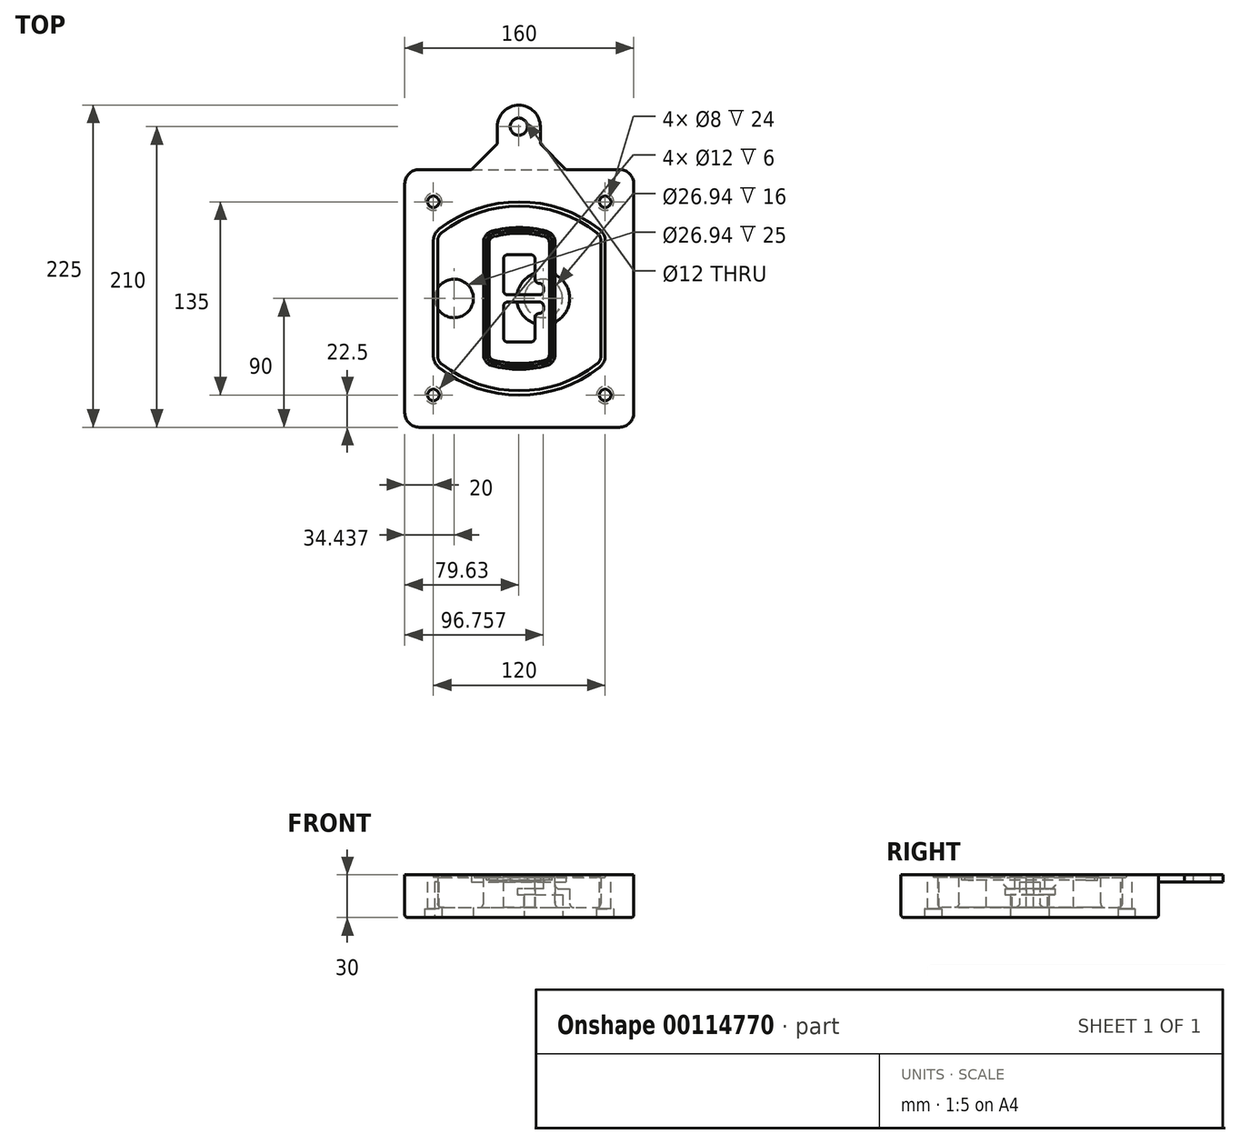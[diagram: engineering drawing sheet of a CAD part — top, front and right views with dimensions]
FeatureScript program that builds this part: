
annotation { "Feature Type Name" : "Feature", "Feature Type Description" : "" }
export const myFeature = defineFeature(function(context is Context, id is Id, definition is map)
    precondition{}
    {
        {
            var Q0;
            Q0=qCreatedBy(makeId("Top.planeOp"),FACE);
            var sketch = newSketch(context, id + "F0", { "sketchPlane" : qUnion([Q0])});
            skPoint(sketch, "E0.rect.middle", {"position": v(0, 0) * mm});
            skLineSegment(sketch, "E1.bottom", {"start": v(-70, -90) * mm, "end": v(70, -90) * mm});
            skLineSegment(sketch, "E1.top", {"start": v(-70, 90) * mm, "end": v(70, 90) * mm});
            skLineSegment(sketch, "E1.left", {"start": v(-80, -80) * mm, "end": v(-80, 80) * mm});
            skLineSegment(sketch, "E1.right", {"start": v(80, -80) * mm, "end": v(80, 80) * mm});
            skLineSegment(sketch, "E2", {"start": v(-80, 90) * mm, "end": v(80, -90) * mm, "construction": true});
            skLineSegment(sketch, "E3", {"start": v(80, 90) * mm, "end": v(-80, -90) * mm, "construction": true});
            skCircle(sketch, "E4", {"center": v(-60, 67.5) * mm, "radius": 4 * mm});
            skCircle(sketch, "E5", {"center": v(60, 67.5) * mm, "radius": 4 * mm});
            skCircle(sketch, "E6", {"center": v(60, -67.5) * mm, "radius": 4 * mm});
            skCircle(sketch, "E7", {"center": v(-60, -67.5) * mm, "radius": 4 * mm});
            skLineSegment(sketch, "E8", {"start": v(-60, 67.5) * mm, "end": v(60, 67.5) * mm, "construction": true});
            skLineSegment(sketch, "E9", {"start": v(60, 67.5) * mm, "end": v(60, -67.5) * mm, "construction": true});
            skLineSegment(sketch, "E10", {"start": v(60, -67.5) * mm, "end": v(-60, -67.5) * mm, "construction": true});
            skLineSegment(sketch, "E11", {"start": v(-60, -67.5) * mm, "end": v(-60, 67.5) * mm, "construction": true});
            skLineSegment(sketch, "E12", {"start": v(-60, 40.3) * mm, "end": v(-60, -40.3) * mm});
            skLineSegment(sketch, "E13", {"start": v(60, 40.3) * mm, "end": v(60, -40.3) * mm});
            skArc(sketch, "E14", {"start": v(56.15, 48.18) * mm, "mid": v(0, 67.5) * mm, "end": v(-56.15, 48.18) * mm});
            skArc(sketch, "E15", {"start": v(-56.15, -48.18) * mm, "mid": v(0, -67.5) * mm, "end": v(56.15, -48.18) * mm});
            skLineSegment(sketch, "E16", {"start": v(-60, 0) * mm, "end": v(60, 0) * mm, "construction": true});
            skPoint(sketch, "E17.visualSharp", {"position": v(-60, -45) * mm});
            skArc(sketch, "E17.filletArc", {"start": v(-60, -40.3) * mm, "mid": v(-58.99, -44.68) * mm, "end": v(-56.15, -48.18) * mm});
            skPoint(sketch, "E18.visualSharp", {"position": v(-60, 45) * mm});
            skArc(sketch, "E18.filletArc", {"start": v(-56.15, 48.18) * mm, "mid": v(-58.99, 44.68) * mm, "end": v(-60, 40.3) * mm});
            skPoint(sketch, "E19.visualSharp", {"position": v(60, 45) * mm});
            skArc(sketch, "E19.filletArc", {"start": v(60, 40.3) * mm, "mid": v(58.99, 44.68) * mm, "end": v(56.15, 48.18) * mm});
            skPoint(sketch, "E20.visualSharp", {"position": v(60, -45) * mm});
            skArc(sketch, "E20.filletArc", {"start": v(56.15, -48.18) * mm, "mid": v(58.99, -44.68) * mm, "end": v(60, -40.3) * mm});
            skPoint(sketch, "E21.visualSharp", {"position": v(-80, 90) * mm});
            skArc(sketch, "E21.filletArc", {"start": v(-70, 90) * mm, "mid": v(-77.07, 87.07) * mm, "end": v(-80, 80) * mm});
            skPoint(sketch, "E22.visualSharp", {"position": v(80, 90) * mm});
            skArc(sketch, "E22.filletArc", {"start": v(80, 80) * mm, "mid": v(77.07, 87.07) * mm, "end": v(70, 90) * mm});
            skPoint(sketch, "E23.visualSharp", {"position": v(80, -90) * mm});
            skArc(sketch, "E23.filletArc", {"start": v(70, -90) * mm, "mid": v(77.07, -87.07) * mm, "end": v(80, -80) * mm});
            skPoint(sketch, "E24.visualSharp", {"position": v(-80, -90) * mm});
            skArc(sketch, "E24.filletArc", {"start": v(-80, -80) * mm, "mid": v(-77.07, -87.07) * mm, "end": v(-70, -90) * mm});
            skArc(sketch, "E25.0", {"start": v(57, 40.3) * mm, "mid": v(56.3, 43.36) * mm, "end": v(54.3, 45.81) * mm});
            skLineSegment(sketch, "E25.1", {"start": v(57, 40.3) * mm, "end": v(57, -40.3) * mm});
            skArc(sketch, "E25.2", {"start": v(54.3, -45.81) * mm, "mid": v(56.3, -43.36) * mm, "end": v(57, -40.3) * mm});
            skArc(sketch, "E25.3", {"start": v(-54.3, -45.81) * mm, "mid": v(0, -64.5) * mm, "end": v(54.3, -45.81) * mm});
            skArc(sketch, "E25.4", {"start": v(-57, -40.3) * mm, "mid": v(-56.3, -43.36) * mm, "end": v(-54.3, -45.81) * mm});
            skArc(sketch, "E25.5", {"start": v(54.3, 45.81) * mm, "mid": v(0, 64.5) * mm, "end": v(-54.3, 45.81) * mm});
            skLineSegment(sketch, "E25.6", {"start": v(-57, 40.3) * mm, "end": v(-57, -40.3) * mm});
            skArc(sketch, "E25.7", {"start": v(-54.3, 45.81) * mm, "mid": v(-56.3, 43.36) * mm, "end": v(-57, 40.3) * mm});
            skArc(sketch, "E26.0", {"start": v(-58.62, 51.33) * mm, "mid": v(-62.58, 46.43) * mm, "end": v(-64, 40.3) * mm});
            skArc(sketch, "E26.1", {"start": v(58.62, 51.33) * mm, "mid": v(0, 71.5) * mm, "end": v(-58.62, 51.33) * mm});
            skArc(sketch, "E26.2", {"start": v(64, 40.3) * mm, "mid": v(62.58, 46.43) * mm, "end": v(58.62, 51.33) * mm});
            skLineSegment(sketch, "E26.3", {"start": v(64, 40.3) * mm, "end": v(64, -40.3) * mm});
            skArc(sketch, "E26.4", {"start": v(58.62, -51.33) * mm, "mid": v(62.58, -46.43) * mm, "end": v(64, -40.3) * mm});
            skLineSegment(sketch, "E26.5", {"start": v(-64, 40.3) * mm, "end": v(-64, -40.3) * mm});
            skArc(sketch, "E26.6", {"start": v(-58.62, -51.33) * mm, "mid": v(0, -71.5) * mm, "end": v(58.62, -51.33) * mm});
            skArc(sketch, "E26.7", {"start": v(-64, -40.3) * mm, "mid": v(-62.58, -46.43) * mm, "end": v(-58.62, -51.33) * mm});
            skSolve(sketch);
        }
        {
            var Q0;
            Q0=makeQuery(id+"F0.imprint","IMPRINT",FACE,{"disambiguationData":[TD([[makeQuery(id+"F0.imprint","IMPRINT",EDGE,{"derivedFrom":sQuery(id+"F0.wireOp",EDGE,"E1.bottom")}),1.0]])]});
            var Q1;
            Q1=makeQuery(id+"F0.imprint","IMPRINT",FACE,{"disambiguationData":[TD([[makeQuery(id+"F0.imprint","IMPRINT",EDGE,{"derivedFrom":sQuery(id+"F0.wireOp",EDGE,"E12")}),1.0]])]});
            var Q2;
            Q2=makeQuery(id+"F0.imprint","IMPRINT",FACE,{"disambiguationData":[TD([[makeQuery(id+"F0.imprint","IMPRINT",EDGE,{"derivedFrom":sQuery(id+"F0.wireOp",EDGE,"E25.0")}),1.0]])]});
            var Q3;
            Q3=makeQuery(id+"F0.imprint","IMPRINT",FACE,{"disambiguationData":[TD([[makeQuery(id+"F0.imprint","IMPRINT",EDGE,{"derivedFrom":sQuery(id+"F0.wireOp",EDGE,"E12")}),-1.0]])]});
            var Q4;
            Q4 = qSketchRegion(id + "F16", true);
            extrude(context, id + "F1", {"entities" : qUnion([Q0, Q1, Q2, Q3, Q4]), "oppositeDirection" : true, "depth" : 25 * mm});
        }
        {
            var Q0;
            Q0=makeQuery(id+"F0.imprint","IMPRINT",FACE,{"disambiguationData":[TD([[makeQuery(id+"F0.imprint","IMPRINT",EDGE,{"derivedFrom":sQuery(id+"F0.wireOp",EDGE,"E12")}),1.0]])]});
            extrude(context, id + "F2", {"entities" : qUnion([Q0]), "operationType" : NewBodyOperationType.ADD, "depth" : 3 * mm});
        }
        {
            var Q0;
            Q0=makeQuery(id+"F0.imprint","IMPRINT",FACE,{"disambiguationData":[TD([[makeQuery(id+"F0.imprint","IMPRINT",EDGE,{"derivedFrom":sQuery(id+"F0.wireOp",EDGE,"E25.0")}),1.0]])]});
            extrude(context, id + "F3", {"entities" : qUnion([Q0]), "operationType" : NewBodyOperationType.REMOVE, "oppositeDirection" : true, "depth" : 18 * mm});
        }
        {
            var Q0;
            Q0=makeQuery(id+"F2.opExtrude","CAP_FACE",FACE,{"disambiguationData":[OSD([sQuery(id+"F0.wireOp",EDGE,"E12"),sQuery(id+"F0.wireOp",EDGE,"E13"),sQuery(id+"F0.wireOp",EDGE,"E14"),sQuery(id+"F0.wireOp",EDGE,"E15"),sQuery(id+"F0.wireOp",EDGE,"E17.filletArc"),sQuery(id+"F0.wireOp",EDGE,"E18.filletArc"),sQuery(id+"F0.wireOp",EDGE,"E19.filletArc"),sQuery(id+"F0.wireOp",EDGE,"E20.filletArc"),sQuery(id+"F0.wireOp",EDGE,"E25.0"),sQuery(id+"F0.wireOp",EDGE,"E25.1"),sQuery(id+"F0.wireOp",EDGE,"E25.2"),sQuery(id+"F0.wireOp",EDGE,"E25.3"),sQuery(id+"F0.wireOp",EDGE,"E25.4"),sQuery(id+"F0.wireOp",EDGE,"E25.5"),sQuery(id+"F0.wireOp",EDGE,"E25.6"),sQuery(id+"F0.wireOp",EDGE,"E25.7")])],"isStart":false});
            var sketch = newSketch(context, id + "F4", { "sketchPlane" : qUnion([Q0])});
            skArc(sketch, "E27.0", {"start": v(-19.08, -46.97) * mm, "mid": v(0, -49.5) * mm, "end": v(19.08, -46.97) * mm});
            skArc(sketch, "E28.0", {"start": v(19.08, 46.97) * mm, "mid": v(0, 49.5) * mm, "end": v(-19.08, 46.97) * mm});
            skLineSegment(sketch, "E29", {"start": v(-25, 39.25) * mm, "end": v(-25, -39.25) * mm});
            skLineSegment(sketch, "E30", {"start": v(25, 39.25) * mm, "end": v(25, -39.25) * mm});
            skLineSegment(sketch, "E31", {"start": v(-25, 45.1) * mm, "end": v(25, 45.1) * mm, "construction": true});
            skLineSegment(sketch, "E32", {"start": v(-25, -45.1) * mm, "end": v(25, -45.1) * mm, "construction": true});
            skPoint(sketch, "E33.visualSharp", {"position": v(-25, 45.1) * mm});
            skArc(sketch, "E33.filletArc", {"start": v(-19.08, 46.97) * mm, "mid": v(-23.35, 44.11) * mm, "end": v(-25, 39.25) * mm});
            skPoint(sketch, "E34.visualSharp", {"position": v(25, 45.1) * mm});
            skArc(sketch, "E34.filletArc", {"start": v(25, 39.25) * mm, "mid": v(23.35, 44.11) * mm, "end": v(19.08, 46.97) * mm});
            skPoint(sketch, "E35.visualSharp", {"position": v(25, -45.1) * mm});
            skArc(sketch, "E35.filletArc", {"start": v(19.08, -46.97) * mm, "mid": v(23.35, -44.11) * mm, "end": v(25, -39.25) * mm});
            skPoint(sketch, "E36.visualSharp", {"position": v(-25, -45.1) * mm});
            skArc(sketch, "E36.filletArc", {"start": v(-25, -39.25) * mm, "mid": v(-23.35, -44.11) * mm, "end": v(-19.08, -46.97) * mm});
            skArc(sketch, "E37.0", {"start": v(54.3, 45.81) * mm, "mid": v(0, 64.5) * mm, "end": v(-54.3, 45.81) * mm});
            skArc(sketch, "E37.1", {"start": v(-54.3, 45.81) * mm, "mid": v(-56.3, 43.36) * mm, "end": v(-57, 40.3) * mm});
            skLineSegment(sketch, "E37.2", {"start": v(-57, 40.3) * mm, "end": v(-57, -40.3) * mm});
            skArc(sketch, "E37.3", {"start": v(-57, -40.3) * mm, "mid": v(-56.3, -43.36) * mm, "end": v(-54.3, -45.81) * mm});
            skArc(sketch, "E37.4", {"start": v(-54.3, -45.81) * mm, "mid": v(0, -64.5) * mm, "end": v(54.3, -45.81) * mm});
            skArc(sketch, "E37.5", {"start": v(54.3, -45.81) * mm, "mid": v(56.3, -43.36) * mm, "end": v(57, -40.3) * mm});
            skLineSegment(sketch, "E37.6", {"start": v(57, 40.3) * mm, "end": v(57, -40.3) * mm});
            skArc(sketch, "E37.7", {"start": v(57, 40.3) * mm, "mid": v(56.3, 43.36) * mm, "end": v(54.3, 45.81) * mm});
            skLineSegment(sketch, "E38.0", {"start": v(23, 39.25) * mm, "end": v(23, -39.25) * mm});
            skArc(sketch, "E38.1", {"start": v(18.56, -45.04) * mm, "mid": v(21.76, -42.9) * mm, "end": v(23, -39.25) * mm});
            skArc(sketch, "E38.2", {"start": v(-18.56, -45.04) * mm, "mid": v(0, -47.5) * mm, "end": v(18.56, -45.04) * mm});
            skArc(sketch, "E38.3", {"start": v(-23, -39.25) * mm, "mid": v(-21.76, -42.9) * mm, "end": v(-18.56, -45.04) * mm});
            skLineSegment(sketch, "E38.4", {"start": v(-23, 39.25) * mm, "end": v(-23, -39.25) * mm});
            skArc(sketch, "E38.5", {"start": v(23, 39.25) * mm, "mid": v(21.76, 42.9) * mm, "end": v(18.56, 45.04) * mm});
            skArc(sketch, "E38.6", {"start": v(-18.56, 45.04) * mm, "mid": v(-21.76, 42.9) * mm, "end": v(-23, 39.25) * mm});
            skArc(sketch, "E38.7", {"start": v(18.56, 45.04) * mm, "mid": v(0, 47.5) * mm, "end": v(-18.56, 45.04) * mm});
            skArc(sketch, "E39.0", {"start": v(21, 39.25) * mm, "mid": v(20.18, 41.68) * mm, "end": v(18.04, 43.1) * mm});
            skLineSegment(sketch, "E39.1", {"start": v(21, 39.25) * mm, "end": v(21, -39.25) * mm});
            skArc(sketch, "E39.2", {"start": v(18.04, -43.1) * mm, "mid": v(20.18, -41.68) * mm, "end": v(21, -39.25) * mm});
            skArc(sketch, "E39.3", {"start": v(-18.04, -43.1) * mm, "mid": v(0, -45.5) * mm, "end": v(18.04, -43.1) * mm});
            skArc(sketch, "E39.4", {"start": v(-21, -39.25) * mm, "mid": v(-20.18, -41.68) * mm, "end": v(-18.04, -43.1) * mm});
            skArc(sketch, "E39.5", {"start": v(18.04, 43.1) * mm, "mid": v(0, 45.5) * mm, "end": v(-18.04, 43.1) * mm});
            skLineSegment(sketch, "E39.6", {"start": v(-21, 39.25) * mm, "end": v(-21, -39.25) * mm});
            skArc(sketch, "E39.7", {"start": v(-18.04, 43.1) * mm, "mid": v(-20.18, 41.68) * mm, "end": v(-21, 39.25) * mm});
            skLineSegment(sketch, "E40", {"start": v(-25, 0) * mm, "end": v(25, 0) * mm, "construction": true});
            skLineSegment(sketch, "E41", {"start": v(-11, 5.5) * mm, "end": v(-11, 27.5) * mm});
            skLineSegment(sketch, "E42", {"start": v(-8, 30.5) * mm, "end": v(8, 30.5) * mm});
            skLineSegment(sketch, "E43", {"start": v(11, 27.5) * mm, "end": v(11, 13.5) * mm});
            skLineSegment(sketch, "E44", {"start": v(14, 10.5) * mm, "end": v(14, 10.5) * mm});
            skLineSegment(sketch, "E45", {"start": v(17, 7.5) * mm, "end": v(17, 5.5) * mm});
            skLineSegment(sketch, "E46", {"start": v(14, 2.5) * mm, "end": v(-8, 2.5) * mm});
            skPoint(sketch, "E47.visualSharp", {"position": v(-11, 30.5) * mm});
            skArc(sketch, "E47.filletArc", {"start": v(-8, 30.5) * mm, "mid": v(-10.12, 29.62) * mm, "end": v(-11, 27.5) * mm});
            skPoint(sketch, "E48.visualSharp", {"position": v(11, 30.5) * mm});
            skArc(sketch, "E48.filletArc", {"start": v(11, 27.5) * mm, "mid": v(10.12, 29.62) * mm, "end": v(8, 30.5) * mm});
            skPoint(sketch, "E49.visualSharp", {"position": v(11, 10.5) * mm});
            skArc(sketch, "E49.filletArc", {"start": v(11, 13.5) * mm, "mid": v(11.88, 11.38) * mm, "end": v(14, 10.5) * mm});
            skPoint(sketch, "E50.visualSharp", {"position": v(17, 10.5) * mm});
            skArc(sketch, "E50.filletArc", {"start": v(17, 7.5) * mm, "mid": v(16.12, 9.62) * mm, "end": v(14, 10.5) * mm});
            skPoint(sketch, "E51.visualSharp", {"position": v(17, 2.5) * mm});
            skArc(sketch, "E51.filletArc", {"start": v(14, 2.5) * mm, "mid": v(16.12, 3.38) * mm, "end": v(17, 5.5) * mm});
            skPoint(sketch, "E52.visualSharp", {"position": v(-11, 2.5) * mm});
            skArc(sketch, "E52.filletArc", {"start": v(-11, 5.5) * mm, "mid": v(-10.12, 3.38) * mm, "end": v(-8, 2.5) * mm});
            skLineSegment(sketch, "E53.0.MirrorCS", {"start": v(14, -2.5) * mm, "end": v(-8, -2.5) * mm});
            skArc(sketch, "E54.0.MirrorCS", {"start": v(-11, -5.5) * mm, "mid": v(-10.12, -3.38) * mm, "end": v(-8, -2.5) * mm});
            skLineSegment(sketch, "E55.0.MirrorCS", {"start": v(-11, -5.5) * mm, "end": v(-11, -27.5) * mm});
            skArc(sketch, "E56.0.MirrorCS", {"start": v(-8, -30.5) * mm, "mid": v(-10.12, -29.62) * mm, "end": v(-11, -27.5) * mm});
            skLineSegment(sketch, "E57.0.MirrorCS", {"start": v(-8, -30.5) * mm, "end": v(8, -30.5) * mm});
            skArc(sketch, "E58.0.MirrorCS", {"start": v(11, -27.5) * mm, "mid": v(10.12, -29.62) * mm, "end": v(8, -30.5) * mm});
            skLineSegment(sketch, "E59.0.MirrorCS", {"start": v(11, -27.5) * mm, "end": v(11, -13.5) * mm});
            skArc(sketch, "E60.0.MirrorCS", {"start": v(11, -13.5) * mm, "mid": v(11.88, -11.38) * mm, "end": v(14, -10.5) * mm});
            skArc(sketch, "E61.0.MirrorCS", {"start": v(17, -7.5) * mm, "mid": v(16.12, -9.62) * mm, "end": v(14, -10.5) * mm});
            skLineSegment(sketch, "E62.0.MirrorCS", {"start": v(17, -7.5) * mm, "end": v(17, -5.5) * mm});
            skArc(sketch, "E63.0.MirrorCS", {"start": v(14, -2.5) * mm, "mid": v(16.12, -3.38) * mm, "end": v(17, -5.5) * mm});
            skSolve(sketch);
        }
        {
            var Q0;
            Q0=makeQuery(id+"F4.imprint","IMPRINT",FACE,{"disambiguationData":[TD([[makeQuery(id+"F4.imprint","IMPRINT",EDGE,{"derivedFrom":sQuery(id+"F4.wireOp",EDGE,"E27.0")}),1.0]])]});
            var Q1;
            Q1=makeQuery(id+"F4.imprint","IMPRINT",FACE,{"disambiguationData":[TD([[makeQuery(id+"F4.imprint","IMPRINT",EDGE,{"derivedFrom":sQuery(id+"F4.wireOp",EDGE,"E38.0")}),-1.0]])]});
            var Q2;
            Q2=makeQuery(id+"F4.imprint","IMPRINT",FACE,{"disambiguationData":[TD([[makeQuery(id+"F4.imprint","IMPRINT",EDGE,{"derivedFrom":sQuery(id+"F4.wireOp",EDGE,"E39.0")}),1.0]])]});
            extrude(context, id + "F5", {"entities" : qUnion([Q0, Q1, Q2]), "operationType" : NewBodyOperationType.ADD, "endBound" : BoundingType.UP_TO_NEXT, "oppositeDirection" : true, "depth" : 25 * mm});
        }
        {
            var Q0;
            Q0=makeQuery(id+"F4.imprint","IMPRINT",FACE,{"disambiguationData":[TD([[makeQuery(id+"F4.imprint","IMPRINT",EDGE,{"derivedFrom":sQuery(id+"F4.wireOp",EDGE,"E38.0")}),-1.0]])]});
            extrude(context, id + "F6", {"entities" : qUnion([Q0]), "operationType" : NewBodyOperationType.REMOVE, "oppositeDirection" : true, "depth" : 2 * mm});
        }
        {
            var Q0;
            Q0=makeQuery(id+"F1.opExtrude","CAP_FACE",FACE,{"disambiguationData":[OSD([sQuery(id+"F0.wireOp",EDGE,"E1.bottom"),sQuery(id+"F0.wireOp",EDGE,"E1.top"),sQuery(id+"F0.wireOp",EDGE,"E1.left"),sQuery(id+"F0.wireOp",EDGE,"E1.right"),sQuery(id+"F0.wireOp",EDGE,"E4"),sQuery(id+"F0.wireOp",EDGE,"E5"),sQuery(id+"F0.wireOp",EDGE,"E6"),sQuery(id+"F0.wireOp",EDGE,"E7"),sQuery(id+"F0.wireOp",EDGE,"E21.filletArc"),sQuery(id+"F0.wireOp",EDGE,"E22.filletArc"),sQuery(id+"F0.wireOp",EDGE,"E23.filletArc"),sQuery(id+"F0.wireOp",EDGE,"E24.filletArc")])],"isStart":false});
            var sketch = newSketch(context, id + "F7", { "sketchPlane" : qUnion([Q0])});
            skCircle(sketch, "E64", {"center": v(16.76, 0) * mm, "radius": 13.47 * mm});
            skCircle(sketch, "E65", {"center": v(-45.56, 0) * mm, "radius": 13.47 * mm});
            skLineSegment(sketch, "E66", {"start": v(80, 0) * mm, "end": v(-80, 0) * mm});
            skCircle(sketch, "E67", {"center": v(16.76, 0) * mm, "radius": 18.47 * mm});
            skCircle(sketch, "E68", {"center": v(60, -67.5) * mm, "radius": 6 * mm});
            skCircle(sketch, "E69", {"center": v(-60, -67.5) * mm, "radius": 6 * mm});
            skCircle(sketch, "E70", {"center": v(-60, 67.5) * mm, "radius": 6 * mm});
            skCircle(sketch, "E71", {"center": v(60, 67.5) * mm, "radius": 6 * mm});
            skSolve(sketch);
        }
        {
            var Q0;
            {var subQ1=sQuery(id+"F7.wireOp",EDGE,"E66");var subQ4=sQuery(id+"F7.wireOp",EDGE,"E64");var subQ6=makeQuery(id+"F7.imprint","INTERSECT",VERTEX,{"disambiguationData":[OD(0.0)],"derivedFrom":[subQ4,subQ1]});Q0=makeQuery(id+"F7.imprint","IMPRINT",FACE,{"disambiguationData":[TD([[makeQuery(id+"F7.imprint","IMPRINT",EDGE,{"disambiguationData":[TD([[subQ6,-1.0]])],"derivedFrom":subQ4}),-1.0]])]});}
            var Q1;
            {var subQ0=sQuery(id+"F7.wireOp",EDGE,"E66");var subQ1=sQuery(id+"F7.wireOp",EDGE,"E64");var subQ3=makeQuery(id+"F7.imprint","INTERSECT",VERTEX,{"disambiguationData":[OD(0.0)],"derivedFrom":[subQ1,subQ0]});Q1=makeQuery(id+"F7.imprint","IMPRINT",FACE,{"disambiguationData":[TD([[makeQuery(id+"F7.imprint","IMPRINT",EDGE,{"disambiguationData":[TD([[subQ3,-1.0]])],"derivedFrom":subQ1}),1.0]])]});}
            var Q2;
            {var subQ0=sQuery(id+"F7.wireOp",EDGE,"E66");var subQ1=sQuery(id+"F7.wireOp",EDGE,"E64");var subQ3=makeQuery(id+"F7.imprint","INTERSECT",VERTEX,{"disambiguationData":[OD(0.0)],"derivedFrom":[subQ1,subQ0]});Q2=makeQuery(id+"F7.imprint","IMPRINT",FACE,{"disambiguationData":[TD([[makeQuery(id+"F7.imprint","IMPRINT",EDGE,{"disambiguationData":[TD([[subQ3,1.0]])],"derivedFrom":subQ1}),1.0]])]});}
            var Q3;
            {var subQ1=sQuery(id+"F7.wireOp",EDGE,"E66");var subQ4=sQuery(id+"F7.wireOp",EDGE,"E64");var subQ6=makeQuery(id+"F7.imprint","INTERSECT",VERTEX,{"disambiguationData":[OD(0.0)],"derivedFrom":[subQ4,subQ1]});Q3=makeQuery(id+"F7.imprint","IMPRINT",FACE,{"disambiguationData":[TD([[makeQuery(id+"F7.imprint","IMPRINT",EDGE,{"disambiguationData":[TD([[subQ6,1.0]])],"derivedFrom":subQ4}),-1.0]])]});}
            extrude(context, id + "F8", {"entities" : qUnion([Q0, Q1, Q2, Q3]), "operationType" : NewBodyOperationType.ADD, "oppositeDirection" : true, "depth" : 20 * mm});
        }
        {
            var Q0;
            {var subQ0=sQuery(id+"F7.wireOp",EDGE,"E66");var subQ1=sQuery(id+"F7.wireOp",EDGE,"E64");var subQ3=makeQuery(id+"F7.imprint","INTERSECT",VERTEX,{"disambiguationData":[OD(0.0)],"derivedFrom":[subQ1,subQ0]});Q0=makeQuery(id+"F7.imprint","IMPRINT",FACE,{"disambiguationData":[TD([[makeQuery(id+"F7.imprint","IMPRINT",EDGE,{"disambiguationData":[TD([[subQ3,-1.0]])],"derivedFrom":subQ1}),1.0]])]});}
            var Q1;
            {var subQ0=sQuery(id+"F7.wireOp",EDGE,"E66");var subQ1=sQuery(id+"F7.wireOp",EDGE,"E64");var subQ3=makeQuery(id+"F7.imprint","INTERSECT",VERTEX,{"disambiguationData":[OD(0.0)],"derivedFrom":[subQ1,subQ0]});Q1=makeQuery(id+"F7.imprint","IMPRINT",FACE,{"disambiguationData":[TD([[makeQuery(id+"F7.imprint","IMPRINT",EDGE,{"disambiguationData":[TD([[subQ3,1.0]])],"derivedFrom":subQ1}),1.0]])]});}
            extrude(context, id + "F9", {"entities" : qUnion([Q0, Q1]), "operationType" : NewBodyOperationType.REMOVE, "oppositeDirection" : true, "depth" : 16 * mm});
        }
        {
            var Q0;
            {var subQ0=sQuery(id+"F7.wireOp",EDGE,"E66");var subQ1=sQuery(id+"F7.wireOp",EDGE,"E65");var subQ3=makeQuery(id+"F7.imprint","INTERSECT",VERTEX,{"disambiguationData":[OD(0.0)],"derivedFrom":[subQ1,subQ0]});Q0=makeQuery(id+"F7.imprint","IMPRINT",FACE,{"disambiguationData":[TD([[makeQuery(id+"F7.imprint","IMPRINT",EDGE,{"disambiguationData":[TD([[subQ3,-1.0]])],"derivedFrom":subQ1}),1.0]])]});}
            var Q1;
            {var subQ0=sQuery(id+"F7.wireOp",EDGE,"E66");var subQ1=sQuery(id+"F7.wireOp",EDGE,"E65");var subQ3=makeQuery(id+"F7.imprint","INTERSECT",VERTEX,{"disambiguationData":[OD(0.0)],"derivedFrom":[subQ1,subQ0]});Q1=makeQuery(id+"F7.imprint","IMPRINT",FACE,{"disambiguationData":[TD([[makeQuery(id+"F7.imprint","IMPRINT",EDGE,{"disambiguationData":[TD([[subQ3,1.0]])],"derivedFrom":subQ1}),1.0]])]});}
            extrude(context, id + "F10", {"entities" : qUnion([Q0, Q1]), "operationType" : NewBodyOperationType.REMOVE, "oppositeDirection" : true, "depth" : 25 * mm});
        }
        {
            var Q0;
            Q0=makeQuery(id+"F7.imprint","IMPRINT",FACE,{"disambiguationData":[TD([[makeQuery(id+"F7.imprint","IMPRINT",EDGE,{"derivedFrom":sQuery(id+"F7.wireOp",EDGE,"E68")}),1.0]])]});
            var Q1;
            Q1=makeQuery(id+"F7.imprint","IMPRINT",FACE,{"disambiguationData":[TD([[makeQuery(id+"F7.imprint","IMPRINT",EDGE,{"derivedFrom":makeQuery(id+"F1.opExtrude","CAP_EDGE",EDGE,{"disambiguationData":[OSD([sQuery(id+"F0.wireOp",EDGE,"E5")])],"isStart":false})}),-1.0]])]});
            var Q2;
            Q2=makeQuery(id+"F7.imprint","IMPRINT",FACE,{"disambiguationData":[TD([[makeQuery(id+"F7.imprint","IMPRINT",EDGE,{"derivedFrom":sQuery(id+"F7.wireOp",EDGE,"E69")}),1.0]])]});
            var Q3;
            Q3=makeQuery(id+"F7.imprint","IMPRINT",FACE,{"disambiguationData":[TD([[makeQuery(id+"F7.imprint","IMPRINT",EDGE,{"derivedFrom":makeQuery(id+"F1.opExtrude","CAP_EDGE",EDGE,{"disambiguationData":[OSD([sQuery(id+"F0.wireOp",EDGE,"E4")])],"isStart":false})}),-1.0]])]});
            var Q4;
            Q4=makeQuery(id+"F7.imprint","IMPRINT",FACE,{"disambiguationData":[TD([[makeQuery(id+"F7.imprint","IMPRINT",EDGE,{"derivedFrom":sQuery(id+"F7.wireOp",EDGE,"E70")}),1.0]])]});
            var Q5;
            Q5=makeQuery(id+"F7.imprint","IMPRINT",FACE,{"disambiguationData":[TD([[makeQuery(id+"F7.imprint","IMPRINT",EDGE,{"derivedFrom":makeQuery(id+"F1.opExtrude","CAP_EDGE",EDGE,{"disambiguationData":[OSD([sQuery(id+"F0.wireOp",EDGE,"E7")])],"isStart":false})}),-1.0]])]});
            var Q6;
            Q6=makeQuery(id+"F7.imprint","IMPRINT",FACE,{"disambiguationData":[TD([[makeQuery(id+"F7.imprint","IMPRINT",EDGE,{"derivedFrom":sQuery(id+"F7.wireOp",EDGE,"E71")}),1.0]])]});
            var Q7;
            Q7=makeQuery(id+"F7.imprint","IMPRINT",FACE,{"disambiguationData":[TD([[makeQuery(id+"F7.imprint","IMPRINT",EDGE,{"derivedFrom":makeQuery(id+"F1.opExtrude","CAP_EDGE",EDGE,{"disambiguationData":[OSD([sQuery(id+"F0.wireOp",EDGE,"E6")])],"isStart":false})}),-1.0]])]});
            extrude(context, id + "F11", {"entities" : qUnion([Q0, Q1, Q2, Q3, Q4, Q5, Q6, Q7]), "operationType" : NewBodyOperationType.REMOVE, "oppositeDirection" : true, "depth" : 6 * mm});
        }
        {
            var Q0;
            Q0=makeQuery(id+"F9.boolean.opBoolean","COPY",FACE,{"derivedFrom":makeQuery(id+"F9.opExtrude","CAP_FACE",FACE,{"disambiguationData":[OSD([sQuery(id+"F7.wireOp",EDGE,"E64")])],"isStart":false})});
            var sketch = newSketch(context, id + "F12", { "sketchPlane" : qUnion([Q0])});
            skArc(sketch, "E72.0", {"start": v(11, 17.55) * mm, "mid": v(2.57, 11.82) * mm, "end": v(-1.54, 2.5) * mm});
            skArc(sketch, "E72.1", {"start": v(-1.54, -2.5) * mm, "mid": v(2.57, -11.82) * mm, "end": v(11, -17.55) * mm});
            skLineSegment(sketch, "E73", {"start": v(-1.54, -2.5) * mm, "end": v(14, -2.5) * mm});
            skLineSegment(sketch, "E74.0", {"start": v(14, 2.5) * mm, "end": v(-1.54, 2.5) * mm});
            skArc(sketch, "E74.1", {"start": v(14, 2.5) * mm, "mid": v(16.12, 3.38) * mm, "end": v(17, 5.5) * mm});
            skLineSegment(sketch, "E74.2", {"start": v(17, 7.5) * mm, "end": v(17, 5.5) * mm});
            skArc(sketch, "E74.3", {"start": v(17, 7.5) * mm, "mid": v(16.12, 9.62) * mm, "end": v(14, 10.5) * mm});
            skArc(sketch, "E74.4", {"start": v(11, 13.5) * mm, "mid": v(11.88, 11.38) * mm, "end": v(14, 10.5) * mm});
            skLineSegment(sketch, "E74.5", {"start": v(11, 17.55) * mm, "end": v(11, 13.5) * mm});
            skLineSegment(sketch, "E74.7", {"start": v(14, -2.5) * mm, "end": v(-1.54, -2.5) * mm});
            skArc(sketch, "E74.8", {"start": v(14, -2.5) * mm, "mid": v(16.12, -3.38) * mm, "end": v(17, -5.5) * mm});
            skLineSegment(sketch, "E74.9", {"start": v(17, -7.5) * mm, "end": v(17, -5.5) * mm});
            skArc(sketch, "E74.10", {"start": v(17, -7.5) * mm, "mid": v(16.12, -9.62) * mm, "end": v(14, -10.5) * mm});
            skArc(sketch, "E74.11", {"start": v(11, -13.5) * mm, "mid": v(11.88, -11.38) * mm, "end": v(14, -10.5) * mm});
            skLineSegment(sketch, "E74.12", {"start": v(11, -17.55) * mm, "end": v(11, -13.5) * mm});
            skPoint(sketch, "E75.orphan", {"position": v(11, -27.5) * mm});
            skPoint(sketch, "E76.orphan", {"position": v(-8, -2.5) * mm});
            skPoint(sketch, "E77.orphan", {"position": v(-8, 2.5) * mm});
            skPoint(sketch, "E78.orphan", {"position": v(11, 27.5) * mm});
            skSolve(sketch);
        }
        {
            var Q0;
            {var subQ7=sQuery(id+"F12.wireOp",EDGE,"E72.0");var subQ14=sQuery(id+"F12.wireOp",EDGE,"E72.1");var subQ16=sQuery(id+"F12.wireOp",EDGE,"E74.1");var subQ18=sQuery(id+"F12.wireOp",EDGE,"E74.8");Q0=qUnion([makeQuery(id+"F12.imprint","IMPRINT",FACE,{"disambiguationData":[TD([[makeQuery(id+"F12.imprint","IMPRINT",EDGE,{"derivedFrom":subQ7}),1.0]])]}),makeQuery(id+"F12.imprint","IMPRINT",FACE,{"disambiguationData":[TD([[makeQuery(id+"F12.imprint","IMPRINT",EDGE,{"derivedFrom":subQ14}),1.0]])]}),makeQuery(id+"F12.imprint","IMPRINT",FACE,{"disambiguationData":[TD([[makeQuery(id+"F12.imprint","IMPRINT",EDGE,{"derivedFrom":subQ16}),1.0]])]}),makeQuery(id+"F12.imprint","IMPRINT",FACE,{"disambiguationData":[TD([[makeQuery(id+"F12.imprint","IMPRINT",EDGE,{"derivedFrom":subQ18}),-1.0]])]})]);}
            var Q1;
            Q1=makeQuery(id+"F5.boolean.opBoolean","SPLIT",FACE,{"disambiguationData":[TD([makeQuery(id+"F5.opExtrude","SWEPT_FACE",FACE,{"disambiguationData":[OSD([sQuery(id+"F4.wireOp",EDGE,"E41")])]})])],"derivedFrom":makeQuery(id+"F3.boolean.opBoolean","COPY",FACE,{"derivedFrom":makeQuery(id+"F3.opExtrude","CAP_FACE",FACE,{"disambiguationData":[OSD([sQuery(id+"F0.wireOp",EDGE,"E25.0"),sQuery(id+"F0.wireOp",EDGE,"E25.1"),sQuery(id+"F0.wireOp",EDGE,"E25.2"),sQuery(id+"F0.wireOp",EDGE,"E25.3"),sQuery(id+"F0.wireOp",EDGE,"E25.4"),sQuery(id+"F0.wireOp",EDGE,"E25.5"),sQuery(id+"F0.wireOp",EDGE,"E25.6"),sQuery(id+"F0.wireOp",EDGE,"E25.7")])],"isStart":false})})});
            extrude(context, id + "F13", {"entities" : qUnion([Q0]), "operationType" : NewBodyOperationType.REMOVE, "endBound" : BoundingType.UP_TO_SURFACE, "endBoundEntityFace" : qUnion([Q1]), "depth" : 25 * mm});
        }
        {
            var Q0;
            Q0=makeQuery(id+"F3.boolean.opBoolean","COPY",EDGE,{"derivedFrom":makeQuery(id+"F3.opExtrude","CAP_EDGE",EDGE,{"disambiguationData":[OSD([sQuery(id+"F0.wireOp",EDGE,"E25.6")])],"isStart":false})});
            var Q1;
            Q1=makeQuery(id+"F8.boolean.opBoolean","INTERSECT",EDGE,{"derivedFrom":[makeQuery(id+"F5.opExtrude","SWEPT_FACE",FACE,{"disambiguationData":[OSD([sQuery(id+"F4.wireOp",EDGE,"E30")])]}),makeQuery(id+"F8.opExtrude","CAP_FACE",FACE,{"disambiguationData":[OSD([sQuery(id+"F7.wireOp",EDGE,"E67")])],"isStart":false})]});
            var Q2;
            Q2=makeQuery(id+"F8.boolean.opBoolean","INTERSECT",EDGE,{"disambiguationData":[OD(1.0)],"derivedFrom":[makeQuery(id+"F5.opExtrude","SWEPT_FACE",FACE,{"disambiguationData":[OSD([sQuery(id+"F4.wireOp",EDGE,"E30")])]}),makeQuery(id+"F8.opExtrude","SWEPT_FACE",FACE,{"disambiguationData":[OSD([sQuery(id+"F7.wireOp",EDGE,"E67")])]})]});
            var Q3;
            {var subQ0=sQuery(id+"F4.wireOp",EDGE,"E30");Q3=makeQuery(id+"F8.boolean.opBoolean","SPLIT",EDGE,{"disambiguationData":[TD([makeQuery(id+"F5.opExtrude","SWEPT_FACE",FACE,{"disambiguationData":[OSD([sQuery(id+"F4.wireOp",EDGE,"E35.filletArc")])]})])],"derivedFrom":makeQuery(id+"F5.opExtrude","CAP_EDGE",EDGE,{"disambiguationData":[OSD([subQ0])],"isStart":false})});}
            var Q4;
            {var subQ0=sQuery(id+"F0.wireOp",EDGE,"E25.7");var subQ1=sQuery(id+"F0.wireOp",EDGE,"E25.1");var subQ2=sQuery(id+"F0.wireOp",EDGE,"E25.6");var subQ3=sQuery(id+"F0.wireOp",EDGE,"E25.5");var subQ4=sQuery(id+"F0.wireOp",EDGE,"E25.4");var subQ5=sQuery(id+"F0.wireOp",EDGE,"E25.0");var subQ6=sQuery(id+"F0.wireOp",EDGE,"E25.2");var subQ7=sQuery(id+"F0.wireOp",EDGE,"E25.3");Q4=makeQuery(id+"F8.boolean.opBoolean","INTERSECT",EDGE,{"derivedFrom":[makeQuery(id+"F5.boolean.opBoolean","SPLIT",FACE,{"disambiguationData":[TD([makeQuery(id+"F2.opExtrude","SWEPT_FACE",FACE,{"disambiguationData":[OSD([subQ5])]})])],"derivedFrom":makeQuery(id+"F3.boolean.opBoolean","COPY",FACE,{"derivedFrom":makeQuery(id+"F3.opExtrude","CAP_FACE",FACE,{"disambiguationData":[OSD([subQ5,subQ1,subQ6,subQ7,subQ4,subQ3,subQ2,subQ0])],"isStart":false})})}),makeQuery(id+"F8.opExtrude","SWEPT_FACE",FACE,{"disambiguationData":[OSD([sQuery(id+"F7.wireOp",EDGE,"E67")])]})]});}
            var Q5;
            Q5=makeQuery(id+"F8.boolean.opBoolean","INTERSECT",EDGE,{"disambiguationData":[OD(0.0)],"derivedFrom":[makeQuery(id+"F5.opExtrude","SWEPT_FACE",FACE,{"disambiguationData":[OSD([sQuery(id+"F4.wireOp",EDGE,"E30")])]}),makeQuery(id+"F8.opExtrude","SWEPT_FACE",FACE,{"disambiguationData":[OSD([sQuery(id+"F7.wireOp",EDGE,"E67")])]})]});
            fillet(context, id + "F14", {"entities" : qUnion([Q0, Q1, Q2, Q3, Q4, Q5]), "radius" : 3 * mm, "tangentPropagation" : true, "allowEdgeOverflow" : false});
        }
        {
            var Q0;
            Q0=makeQuery(id+"F1.opExtrude","CAP_EDGE",EDGE,{"disambiguationData":[OSD([sQuery(id+"F0.wireOp",EDGE,"E1.bottom")])],"isStart":false});
            fillet(context, id + "F15", {"entities" : qUnion([Q0]), "radius" : 2 * mm, "tangentPropagation" : true, "allowEdgeOverflow" : false});
        }
        {
            var Q0;
            {var subQ0=sQuery(id+"F0.wireOp",EDGE,"E22.filletArc");var subQ1=sQuery(id+"F0.wireOp",EDGE,"E7");var subQ2=sQuery(id+"F0.wireOp",EDGE,"E6");var subQ3=sQuery(id+"F0.wireOp",EDGE,"E5");var subQ4=sQuery(id+"F0.wireOp",EDGE,"E4");var subQ5=sQuery(id+"F0.wireOp",EDGE,"E1.bottom");var subQ6=sQuery(id+"F0.wireOp",EDGE,"E21.filletArc");var subQ7=sQuery(id+"F0.wireOp",EDGE,"E1.top");var subQ8=sQuery(id+"F0.wireOp",EDGE,"E1.left");var subQ9=sQuery(id+"F0.wireOp",EDGE,"E1.right");var subQ10=sQuery(id+"F0.wireOp",EDGE,"E23.filletArc");var subQ11=sQuery(id+"F0.wireOp",EDGE,"E24.filletArc");Q0=makeQuery(id+"F2.boolean.opBoolean","SPLIT",FACE,{"disambiguationData":[TD([makeQuery(id+"F1.opExtrude","SWEPT_FACE",FACE,{"disambiguationData":[OSD([subQ5])]})])],"derivedFrom":makeQuery(id+"F1.opExtrude","CAP_FACE",FACE,{"disambiguationData":[OSD([subQ5,subQ7,subQ8,subQ9,subQ4,subQ3,subQ2,subQ1,subQ6,subQ0,subQ10,subQ11])],"isStart":true})});}
            var sketch = newSketch(context, id + "F16", { "sketchPlane" : qUnion([Q0])});
            skSolve(sketch);
        }
        {
            var Q0;
            {var subQ0=sQuery(id+"F0.wireOp",EDGE,"E22.filletArc");var subQ1=sQuery(id+"F0.wireOp",EDGE,"E7");var subQ2=sQuery(id+"F0.wireOp",EDGE,"E6");var subQ3=sQuery(id+"F0.wireOp",EDGE,"E5");var subQ4=sQuery(id+"F0.wireOp",EDGE,"E4");var subQ5=sQuery(id+"F0.wireOp",EDGE,"E1.bottom");var subQ6=sQuery(id+"F0.wireOp",EDGE,"E21.filletArc");var subQ7=sQuery(id+"F0.wireOp",EDGE,"E1.top");var subQ8=sQuery(id+"F0.wireOp",EDGE,"E1.left");var subQ9=sQuery(id+"F0.wireOp",EDGE,"E1.right");var subQ10=sQuery(id+"F0.wireOp",EDGE,"E23.filletArc");var subQ11=sQuery(id+"F0.wireOp",EDGE,"E24.filletArc");Q0=makeQuery(id+"F2.boolean.opBoolean","SPLIT",FACE,{"disambiguationData":[TD([makeQuery(id+"F1.opExtrude","SWEPT_FACE",FACE,{"disambiguationData":[OSD([subQ5])]})])],"derivedFrom":makeQuery(id+"F1.opExtrude","CAP_FACE",FACE,{"disambiguationData":[OSD([subQ5,subQ7,subQ8,subQ9,subQ4,subQ3,subQ2,subQ1,subQ6,subQ0,subQ10,subQ11])],"isStart":true})});}
            var sketch = newSketch(context, id + "F17", { "sketchPlane" : qUnion([Q0])});
            skLineSegment(sketch, "E79", {"start": v(-33.3, 90) * mm, "end": v(-15.3, 108) * mm});
            skLineSegment(sketch, "E80", {"start": v(-15.3, 108) * mm, "end": v(-15.3, 120) * mm});
            skLineSegment(sketch, "E81", {"start": v(14.7, 120) * mm, "end": v(14.7, 108) * mm});
            skLineSegment(sketch, "E82", {"start": v(14.7, 108) * mm, "end": v(32.7, 90) * mm});
            skLineSegment(sketch, "E83", {"start": v(32.7, 90) * mm, "end": v(-0.37, 90) * mm});
            skPoint(sketch, "E83.endSnap0", {"position": v(-0.37, 120) * mm});
            skLineSegment(sketch, "E84", {"start": v(-0.37, 90) * mm, "end": v(-33.3, 90) * mm});
            skCircle(sketch, "E85", {"center": v(-0.37, 120) * mm, "radius": 6 * mm});
            skArc(sketch, "E86", {"start": v(-15.3, 120) * mm, "mid": v(-0.3, 135) * mm, "end": v(14.7, 120) * mm});
            skLineSegment(sketch, "E87", {"start": v(-0.37, 120) * mm, "end": v(-0.37, 90) * mm, "construction": true});
            skSolve(sketch);
        }
        {
            var Q0;
            Q0=makeQuery(id+"F16.imprint","IMPRINT",FACE,{"disambiguationData":[TD([[makeQuery(id+"F16.imprint","IMPRINT",EDGE,{"derivedFrom":makeQuery(id+"F1.opExtrude","CAP_EDGE",EDGE,{"disambiguationData":[OSD([sQuery(id+"F0.wireOp",EDGE,"E1.bottom")])],"isStart":true})}),1.0]])]});
            var sketch = newSketch(context, id + "F18", { "sketchPlane" : qUnion([Q0])});
            skLineSegment(sketch, "E88", {"start": v(28.74, -90.33) * mm, "end": v(10.74, -108.33) * mm});
            skLineSegment(sketch, "E89", {"start": v(10.74, -108.33) * mm, "end": v(10.74, -120.33) * mm});
            skLineSegment(sketch, "E90", {"start": v(-19.26, -120.33) * mm, "end": v(-19.26, -108.33) * mm});
            skLineSegment(sketch, "E91", {"start": v(-19.26, -108.33) * mm, "end": v(-37.26, -90.33) * mm});
            skLineSegment(sketch, "E92", {"start": v(-37.26, -90.33) * mm, "end": v(-3.9, -90.33) * mm});
            skPoint(sketch, "E92.endSnap0", {"position": v(-3.9, -120.33) * mm});
            skLineSegment(sketch, "E93", {"start": v(-3.9, -90.33) * mm, "end": v(28.74, -90.33) * mm});
            skCircle(sketch, "E94", {"center": v(-3.9, -120.33) * mm, "radius": 6 * mm});
            skArc(sketch, "E95", {"start": v(10.74, -120.33) * mm, "mid": v(-4.26, -135.33) * mm, "end": v(-19.26, -120.33) * mm});
            skLineSegment(sketch, "E96", {"start": v(-3.9, -120.33) * mm, "end": v(-3.9, -90.33) * mm, "construction": true});
            skSolve(sketch);
        }
        {
            var Q0;
            {var subQ4=sQuery(id+"F17.wireOp",EDGE,"E83");Q0=makeQuery(id+"F17.imprint","IMPRINT",FACE,{"disambiguationData":[TD([[makeQuery(id+"F17.imprint","IMPRINT",EDGE,{"derivedFrom":subQ4}),-1.0]])]});}
            var Q1;
            Q1=makeQuery(id+"F18.imprint","IMPRINT",FACE,{"disambiguationData":[TD([[makeQuery(id+"F18.imprint","IMPRINT",EDGE,{"derivedFrom":sQuery(id+"F18.wireOp",EDGE,"E88")}),-1.0]])]});
            var Q2;
            Q2=makeQuery(id+"F17.imprint","IMPRINT",FACE,{"disambiguationData":[TD([[makeQuery(id+"F17.imprint","IMPRINT",EDGE,{"derivedFrom":sQuery(id+"F17.wireOp",EDGE,"E79")}),-1.0]])]});
            extrude(context, id + "F19", {"entities" : qUnion([Q0, Q1, Q2]), "operationType" : NewBodyOperationType.ADD, "depth" : 5 * mm});
        }
    });
